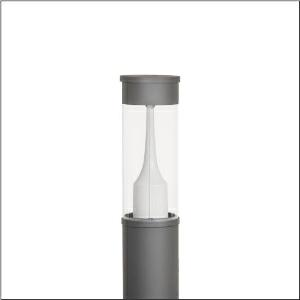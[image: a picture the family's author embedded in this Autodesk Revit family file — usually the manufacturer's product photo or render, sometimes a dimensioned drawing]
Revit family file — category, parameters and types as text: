
# Revit family: city-light_120_iq___pl1_2s_5xa5285rf14h_2286
name_source: partatom
category: Lighting Fixtures
units: mm (PartAtom-declared; Revit-internal decimal feet)

## family parameters
Cut with Voids When Loaded = No
Host = Face
Light Source = No
Part Type = Normal
Room Calculation Point = No
Round Connector Dimension = Use Diameter
Shared = No

## types (1)
- --- (1 x LED, 2970 lm, 18.5 W, 4000K)
    Apparent Load = 19 VA
    CIE Flux Codes = 23 62 94 96 100
    Color Rendering = 70
    Color Temperature = 4000K
    Default Elevation = 1800 mm
    Description = City-Light 120 iQ, bollard luminaire, Module 540 iQ-SR, primary light control with 3 zone facetted reflector, of plastic, silver coated, highly specular, structured, primary optical cover: cover, of PMMA, transparent, partly coated, light distribution: PL1.2s, primary light characteristic: symmetric, LED, High Power LED, rated luminous flux: 2.970lm, luminous efficacy: 161lm/W, light colour: 740, colour temperature: 4000K, control gear: ECG iQ, control: presetting dimming logarithmic, Street-Remote, Auto-Match, Temp-Guard, Lumen-Switch, Night-Set, Smart-Wire, Light-Fading, Desk-Remote (wireless, voltage-free reading and setting of iQ features in the workshop via application-optimized NFC function/RFID function), optimised constant luminous flux control (CLO 2.0), with terminal, 6-pole, max. 2.5mm², mains connection: 230..240V, AC, 50/60Hz, start of lifetime: 19W, end of service life: 20W, reduction: 9W, luminaire housing, cylindrical, of extruded aluminium section, coated, Siteco® metallic grey (DB 702S), length: 1.200mm, diameter: 200mm, Module 540 iQ-SR, traffic white (RAL 9016), equipment: standard, protection rating (complete): IP54, insulation class (complete): insulation class II (safety insulation), certification: CE, ENEC, VDE, packaging unit: 1 piece

Light Distribution: PL1.2s
    Height = 500 mm
    Lamp = 1 x LED
    Lamp Light Flux = 2970 lm
    Lamp Power = 18.5 W
    Lamp count = 1
    Length = 200 mm  [stored 0.656168 ft]
    Luminous efficacy = 161 lm/W
    Manufacturer = Siteco
    ModVariant = No
    Model = 5XA5285RF14H
    Mounting Place = Floor
    Mounting Type = Freestanding
    Number of Poles = 1
    OnlyDefault = Yes
    Power Factor = 1
    Product Name = City-Light 120 iQ | PL1.2s
    Product group = bollard luminaire
    ProductGroupID = 1304
    Protection Class = Protection class II
    Protection Degree = IP 54
    RLX_Detail_Level = 1
    RLX_Emergency_Light_Flux = 0 lm
    RLX_Emergency_Type = 0
    RLX_Emergency_Type_DB = No
    RlxData = <blob elided: 30237 chars, md5=96c30aab>
    Socket = socket
    Standby Power = 0 W
    System Light Flux = 2970 lm
    System Power = 19 W
    Type Comments = factory setting: luminous flux: 100 % | dim-lin: 254 | 385 mA
    Type Image = l_1006922.jpg
    URL = http://relux.com
    VarID = @adj_076777
    Voltage = 0 V
    Weight = 0.00 kg
    Width = 0 mm  [stored 0 ft]

note: [stored X ft] marks values corroborated as IEEE doubles in the binary element streams (Revit-internal decimal feet)

## geometry (parser evidence)
native form markers: Blend x4, Sweep x10
no freeform markers — native parametric forms only
